# Revit family: Little Amp_Bfit 400C_V-1000C_V Boiler and Water Heater
name_source: partatom
category: Mechanical Equipment
units: mm (PartAtom-declared; Revit-internal decimal feet)

## family parameters
Always vertical = Yes
Classification Number = 23.75.00.00
Cut with Voids When Loaded = No
Maintain Annotation Orientation = No
Part Type = Normal
Room Calculation Point = No
Round Connector Dimension = Use Diameter
Shared = No
Work Plane-Based = No

## types (5) — shared parameters
Air Supply X = 5 5/8"
Air Supply Y = 12 1/4"
Boiler Drain = 3/4" NPT Female
Condensate Trap = 1" Pipe
Default Elevation = 0"
Gas Train Ball Valve X = 23 3/16"
Gas Train Ball Valve Y = 27 3/4"
Gas Train X = 23 3/16"
Gas Train Y = 27 3/4"
Height = 38 17/32"
Hydronic Return = 2" NPT Male
Hydronic Supply = 2" NPT Female
Manufacturer = Bryan Steam
Vent X = 16 1/8"
Vent Y = 19 3/4"
Width = 26 1/8"

## per-type parameters (varying)
| type | Air Supply | Air Supply I.D. | Air Supply Length | Air Supply O.D. | Gas Train | Gas Train Ball Valve Dia. | Gas Train Dia. | Length | Vent | Vent I.D. | Vent Length | Vent O.D. |
| AMP 500C/V Boiler and Water Heater | 4" | 4 17/32" | 2 17/32" | 5 1/16" | 3/4" NPT Female | 1 1/2" | 1 1/16" | 36 5/16" | 4" | 4 9/16" | 5 9/16" | 4 31/32" |
| AMP 400C/V Boiler and Water Heater | 4" | 4 17/32" | 2 17/32" | 5 1/16" | 3/4" NPT Female | 1 1/2" | 1 1/16" | 36 5/16" | 4" | 4 9/16" | 5 9/16" | 4 31/32" |
| AMP 650C/V Boiler and Water Heater | 6" | 5 19/32" | 1 7/16" | 5 7/8" | 1" NPT Female | 1 25/32" | 1 5/16" | 52 1/8" | 6" | 6 11/16" | 7 3/32" | 7 1/8" |
| AMP 800C/V Boiler and Water Heater | 6" | 5 19/32" | 1 7/16" | 5 7/8" | 1" NPT Female | 1 25/32" | 1 5/16" | 52 1/8" | 6" | 6 11/16" | 7 3/32" | 7 1/8" |
| AMP 1000C/V Boiler and Water Heater | 6" | 5 19/32" | 1 7/16" | 5 7/8" | 1" NPT Female | 1 25/32" | 1 5/16" | 52 1/8" | 6" | 6 11/16" | 7 3/32" | 7 1/8" |

## geometry (parser evidence)
native form markers: Sweep x2
no freeform markers — native parametric forms only
